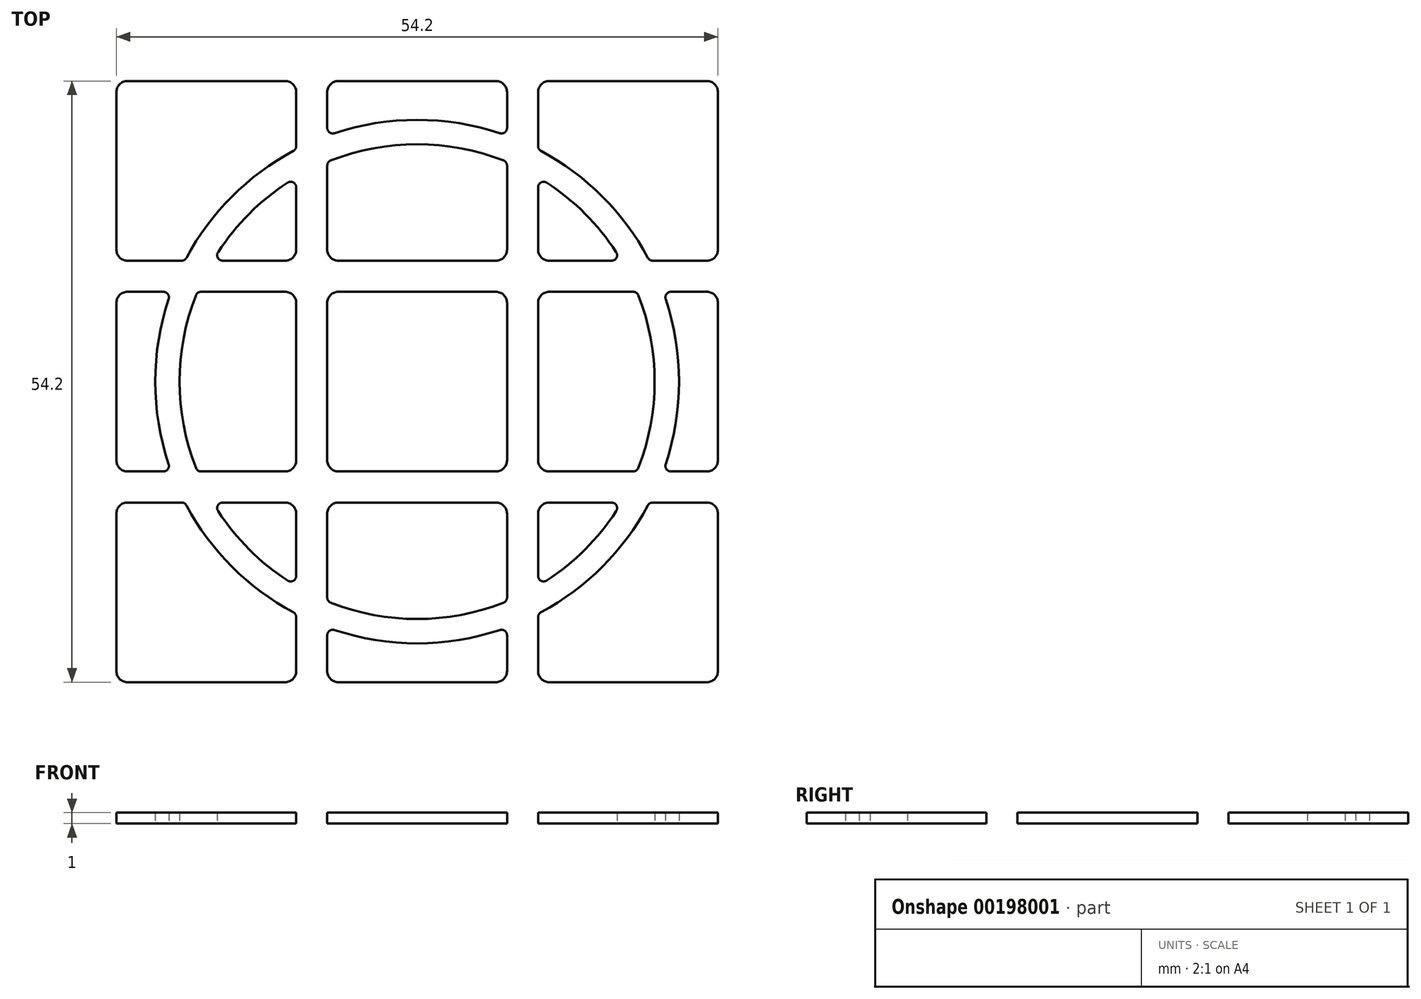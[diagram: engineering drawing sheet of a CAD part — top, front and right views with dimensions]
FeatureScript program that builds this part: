
annotation { "Feature Type Name" : "Feature", "Feature Type Description" : "" }
export const myFeature = defineFeature(function(context is Context, id is Id, definition is map)
    precondition{}
    {
        {
            var Q0;
            Q0=qCreatedBy(makeId("Top.planeOp"),FACE);
            var sketch = newSketch(context, id + "F0", { "sketchPlane" : qUnion([Q0])});
            skLineSegment(sketch, "E0.bottom", {"start": v(28.5, -28.5) * mm, "end": v(-28.5, -28.5) * mm, "construction": true});
            skLineSegment(sketch, "E0.top", {"start": v(28.5, 28.5) * mm, "end": v(-28.5, 28.5) * mm, "construction": true});
            skLineSegment(sketch, "E0.left", {"start": v(28.5, -28.5) * mm, "end": v(28.5, 28.5) * mm, "construction": true});
            skLineSegment(sketch, "E0.right", {"start": v(-28.5, -28.5) * mm, "end": v(-28.5, 28.5) * mm, "construction": true});
            skPoint(sketch, "E0.middle", {"position": v(0, 0) * mm});
            skLineSegment(sketch, "E1", {"start": v(-9.5, 28.5) * mm, "end": v(-9.5, -28.5) * mm, "construction": true});
            skLineSegment(sketch, "E2", {"start": v(9.5, -28.5) * mm, "end": v(9.5, 28.5) * mm, "construction": true});
            skLineSegment(sketch, "E3", {"start": v(-28.5, 9.5) * mm, "end": v(28.5, 9.5) * mm, "construction": true});
            skLineSegment(sketch, "E4", {"start": v(28.5, -9.5) * mm, "end": v(-28.5, -9.5) * mm, "construction": true});
            skArc(sketch, "E5", {"start": v(-11.16, 20.8) * mm, "mid": v(-16.69, 16.69) * mm, "end": v(-20.8, 11.16) * mm});
            skArc(sketch, "E6", {"start": v(-11.67, 17.94) * mm, "mid": v(-15.13, 15.13) * mm, "end": v(-17.94, 11.67) * mm});
            skLineSegment(sketch, "E7.bottom", {"start": v(-26.1, 27.1) * mm, "end": v(-11.9, 27.1) * mm});
            skLineSegment(sketch, "E7.top", {"start": v(-26.1, 10.9) * mm, "end": v(-21.23, 10.9) * mm});
            skLineSegment(sketch, "E7.left", {"start": v(-27.1, 26.1) * mm, "end": v(-27.1, 11.9) * mm});
            skLineSegment(sketch, "E7.right", {"start": v(-10.9, 26.1) * mm, "end": v(-10.9, 21.23) * mm});
            skLineSegment(sketch, "E8.bottom", {"start": v(-26.1, 8.1) * mm, "end": v(-22.87, 8.1) * mm});
            skLineSegment(sketch, "E8.top", {"start": v(-26.1, -8.1) * mm, "end": v(-22.87, -8.1) * mm});
            skLineSegment(sketch, "E8.left", {"start": v(-27.1, 7.1) * mm, "end": v(-27.1, -7.1) * mm});
            skLineSegment(sketch, "E8.right", {"start": v(-10.9, 7.1) * mm, "end": v(-10.9, -7.1) * mm});
            skPoint(sketch, "E9.visualSharp", {"position": v(-27.1, 27.1) * mm});
            skArc(sketch, "E9.filletArc", {"start": v(-26.1, 27.1) * mm, "mid": v(-26.8, 26.8) * mm, "end": v(-27.1, 26.1) * mm});
            skPoint(sketch, "E10.visualSharp", {"position": v(-10.9, 27.1) * mm});
            skArc(sketch, "E10.filletArc", {"start": v(-10.9, 26.1) * mm, "mid": v(-11.2, 26.8) * mm, "end": v(-11.9, 27.1) * mm});
            skPoint(sketch, "E11.visualSharp", {"position": v(-10.9, 10.9) * mm});
            skArc(sketch, "E11.filletArc", {"start": v(-11.9, 10.9) * mm, "mid": v(-11.2, 11.2) * mm, "end": v(-10.9, 11.9) * mm});
            skPoint(sketch, "E12.visualSharp", {"position": v(-27.1, 10.9) * mm});
            skArc(sketch, "E12.filletArc", {"start": v(-27.1, 11.9) * mm, "mid": v(-26.8, 11.2) * mm, "end": v(-26.1, 10.9) * mm});
            skPoint(sketch, "E13.visualSharp", {"position": v(-27.1, 8.1) * mm});
            skArc(sketch, "E13.filletArc", {"start": v(-26.1, 8.1) * mm, "mid": v(-26.8, 7.8) * mm, "end": v(-27.1, 7.1) * mm});
            skPoint(sketch, "E14.visualSharp", {"position": v(-27.1, -8.1) * mm});
            skArc(sketch, "E14.filletArc", {"start": v(-27.1, -7.1) * mm, "mid": v(-26.8, -7.8) * mm, "end": v(-26.1, -8.1) * mm});
            skPoint(sketch, "E15.visualSharp", {"position": v(-10.9, -8.1) * mm});
            skArc(sketch, "E15.filletArc", {"start": v(-11.9, -8.1) * mm, "mid": v(-11.2, -7.8) * mm, "end": v(-10.9, -7.1) * mm});
            skPoint(sketch, "E16.visualSharp", {"position": v(-10.9, 8.1) * mm});
            skArc(sketch, "E16.filletArc", {"start": v(-10.9, 7.1) * mm, "mid": v(-11.2, 7.8) * mm, "end": v(-11.9, 8.1) * mm});
            skLineSegment(sketch, "E17.trimOffspring", {"start": v(-10.9, 17.52) * mm, "end": v(-10.9, 11.9) * mm});
            skLineSegment(sketch, "E18.trimOffspring", {"start": v(-19.47, -8.1) * mm, "end": v(-11.9, -8.1) * mm});
            skLineSegment(sketch, "E19.trimOffspring", {"start": v(-19.47, 8.1) * mm, "end": v(-11.9, 8.1) * mm});
            skLineSegment(sketch, "E20.trimOffspring", {"start": v(-17.52, 10.9) * mm, "end": v(-11.9, 10.9) * mm});
            skArc(sketch, "E21.trimOffspring", {"start": v(-19.93, 7.78) * mm, "mid": v(-21.4, 0) * mm, "end": v(-19.93, -7.78) * mm});
            skArc(sketch, "E22.trimOffspring", {"start": v(-22.4, 7.44) * mm, "mid": v(-23.6, 0) * mm, "end": v(-22.4, -7.44) * mm});
            skPoint(sketch, "E23.visualSharp", {"position": v(-20.93, 10.9) * mm});
            skArc(sketch, "E23.filletArc", {"start": v(-21.23, 10.9) * mm, "mid": v(-20.98, 10.97) * mm, "end": v(-20.8, 11.16) * mm});
            skPoint(sketch, "E24.visualSharp", {"position": v(-10.9, 20.93) * mm});
            skArc(sketch, "E24.filletArc", {"start": v(-11.16, 20.8) * mm, "mid": v(-10.97, 20.98) * mm, "end": v(-10.9, 21.23) * mm});
            skPoint(sketch, "E25.visualSharp", {"position": v(-19.8, 8.1) * mm});
            skArc(sketch, "E25.filletArc", {"start": v(-19.47, 8.1) * mm, "mid": v(-19.75, 8.01) * mm, "end": v(-19.93, 7.78) * mm});
            skPoint(sketch, "E26.visualSharp", {"position": v(-19.8, -8.1) * mm});
            skArc(sketch, "E26.filletArc", {"start": v(-19.93, -7.78) * mm, "mid": v(-19.75, -8.01) * mm, "end": v(-19.47, -8.1) * mm});
            skPoint(sketch, "E27.visualSharp", {"position": v(-18.42, 10.9) * mm});
            skArc(sketch, "E27.filletArc", {"start": v(-17.94, 11.67) * mm, "mid": v(-17.96, 11.16) * mm, "end": v(-17.52, 10.9) * mm});
            skPoint(sketch, "E28.visualSharp", {"position": v(-10.9, 18.42) * mm});
            skArc(sketch, "E28.filletArc", {"start": v(-10.9, 17.52) * mm, "mid": v(-11.16, 17.96) * mm, "end": v(-11.67, 17.94) * mm});
            skPoint(sketch, "E29.visualSharp", {"position": v(-22.17, 8.1) * mm});
            skArc(sketch, "E29.filletArc", {"start": v(-22.4, 7.44) * mm, "mid": v(-22.46, 7.9) * mm, "end": v(-22.87, 8.1) * mm});
            skPoint(sketch, "E30.visualSharp", {"position": v(-22.17, -8.1) * mm});
            skArc(sketch, "E30.filletArc", {"start": v(-22.87, -8.1) * mm, "mid": v(-22.46, -7.9) * mm, "end": v(-22.4, -7.44) * mm});
            skArc(sketch, "E31.1.0", {"start": v(-20.8, -11.16) * mm, "mid": v(-16.69, -16.69) * mm, "end": v(-11.16, -20.8) * mm});
            skLineSegment(sketch, "E31.1.1", {"start": v(8.1, -19.47) * mm, "end": v(8.1, -11.9) * mm});
            skLineSegment(sketch, "E31.1.2", {"start": v(-27.1, -26.1) * mm, "end": v(-27.1, -11.9) * mm});
            skPoint(sketch, "E31.1.3", {"position": v(-8.1, -10.9) * mm});
            skLineSegment(sketch, "E31.1.4", {"start": v(-26.1, -27.1) * mm, "end": v(-11.9, -27.1) * mm});
            skArc(sketch, "E31.1.5", {"start": v(-17.94, -11.67) * mm, "mid": v(-15.13, -15.13) * mm, "end": v(-11.67, -17.94) * mm});
            skLineSegment(sketch, "E31.1.6", {"start": v(-8.1, -19.47) * mm, "end": v(-8.1, -11.9) * mm});
            skArc(sketch, "E31.1.7", {"start": v(-7.78, -19.93) * mm, "mid": v(0, -21.4) * mm, "end": v(7.78, -19.93) * mm});
            skPoint(sketch, "E31.1.8", {"position": v(-8.1, -22.17) * mm});
            skLineSegment(sketch, "E31.1.9", {"start": v(-10.9, -26.1) * mm, "end": v(-10.9, -21.23) * mm});
            skPoint(sketch, "E31.1.10", {"position": v(8.1, -19.8) * mm});
            skPoint(sketch, "E31.1.11", {"position": v(-8.1, -27.1) * mm});
            skLineSegment(sketch, "E31.1.12", {"start": v(-10.9, -17.52) * mm, "end": v(-10.9, -11.9) * mm});
            skLineSegment(sketch, "E31.1.13", {"start": v(-7.1, -27.1) * mm, "end": v(7.1, -27.1) * mm});
            skPoint(sketch, "E31.1.14", {"position": v(-27.1, -10.9) * mm});
            skPoint(sketch, "E31.1.15", {"position": v(-20.93, -10.9) * mm});
            skPoint(sketch, "E31.1.16", {"position": v(-10.9, -10.9) * mm});
            skPoint(sketch, "E31.1.17", {"position": v(8.1, -27.1) * mm});
            skLineSegment(sketch, "E31.1.18", {"start": v(-7.1, -10.9) * mm, "end": v(7.1, -10.9) * mm});
            skPoint(sketch, "E31.1.19", {"position": v(-10.9, -20.93) * mm});
            skPoint(sketch, "E31.1.20", {"position": v(-10.9, -18.42) * mm});
            skPoint(sketch, "E31.1.21", {"position": v(-18.42, -10.9) * mm});
            skPoint(sketch, "E31.1.22", {"position": v(8.1, -10.9) * mm});
            skLineSegment(sketch, "E31.1.23", {"start": v(8.1, -26.1) * mm, "end": v(8.1, -22.87) * mm});
            skLineSegment(sketch, "E31.1.24", {"start": v(-8.1, -26.1) * mm, "end": v(-8.1, -22.87) * mm});
            skLineSegment(sketch, "E31.1.25", {"start": v(-26.1, -10.9) * mm, "end": v(-21.23, -10.9) * mm});
            skArc(sketch, "E31.1.26", {"start": v(-7.44, -22.4) * mm, "mid": v(0, -23.6) * mm, "end": v(7.44, -22.4) * mm});
            skLineSegment(sketch, "E31.1.27", {"start": v(-17.52, -10.9) * mm, "end": v(-11.9, -10.9) * mm});
            skPoint(sketch, "E31.1.28", {"position": v(-27.1, -27.1) * mm});
            skPoint(sketch, "E31.1.29", {"position": v(-8.1, -19.8) * mm});
            skPoint(sketch, "E31.1.30", {"position": v(-10.9, -27.1) * mm});
            skPoint(sketch, "E31.1.31", {"position": v(8.1, -22.17) * mm});
            skArc(sketch, "E31.1.32", {"start": v(8.1, -11.9) * mm, "mid": v(7.8, -11.2) * mm, "end": v(7.1, -10.9) * mm});
            skArc(sketch, "E31.1.33", {"start": v(7.1, -27.1) * mm, "mid": v(7.8, -26.8) * mm, "end": v(8.1, -26.1) * mm});
            skArc(sketch, "E31.1.34", {"start": v(-11.9, -27.1) * mm, "mid": v(-11.2, -26.8) * mm, "end": v(-10.9, -26.1) * mm});
            skArc(sketch, "E31.1.35", {"start": v(-10.9, -11.9) * mm, "mid": v(-11.2, -11.2) * mm, "end": v(-11.9, -10.9) * mm});
            skArc(sketch, "E31.1.36", {"start": v(-8.1, -26.1) * mm, "mid": v(-7.8, -26.8) * mm, "end": v(-7.1, -27.1) * mm});
            skArc(sketch, "E31.1.37", {"start": v(-7.1, -10.9) * mm, "mid": v(-7.8, -11.2) * mm, "end": v(-8.1, -11.9) * mm});
            skArc(sketch, "E31.1.38", {"start": v(-27.1, -26.1) * mm, "mid": v(-26.8, -26.8) * mm, "end": v(-26.1, -27.1) * mm});
            skArc(sketch, "E31.1.39", {"start": v(-26.1, -10.9) * mm, "mid": v(-26.8, -11.2) * mm, "end": v(-27.1, -11.9) * mm});
            skArc(sketch, "E31.1.40", {"start": v(8.1, -22.87) * mm, "mid": v(7.9, -22.46) * mm, "end": v(7.44, -22.4) * mm});
            skArc(sketch, "E31.1.41", {"start": v(-11.67, -17.94) * mm, "mid": v(-11.16, -17.96) * mm, "end": v(-10.9, -17.52) * mm});
            skArc(sketch, "E31.1.42", {"start": v(-17.52, -10.9) * mm, "mid": v(-17.96, -11.16) * mm, "end": v(-17.94, -11.67) * mm});
            skArc(sketch, "E31.1.43", {"start": v(-7.44, -22.4) * mm, "mid": v(-7.9, -22.46) * mm, "end": v(-8.1, -22.87) * mm});
            skArc(sketch, "E31.1.44", {"start": v(-10.9, -21.23) * mm, "mid": v(-10.97, -20.98) * mm, "end": v(-11.16, -20.8) * mm});
            skArc(sketch, "E31.1.45", {"start": v(-20.8, -11.16) * mm, "mid": v(-20.98, -10.97) * mm, "end": v(-21.23, -10.9) * mm});
            skArc(sketch, "E31.1.46", {"start": v(7.78, -19.93) * mm, "mid": v(8.01, -19.75) * mm, "end": v(8.1, -19.47) * mm});
            skArc(sketch, "E31.1.47", {"start": v(-8.1, -19.47) * mm, "mid": v(-8.01, -19.75) * mm, "end": v(-7.78, -19.93) * mm});
            skArc(sketch, "E31.2.0", {"start": v(11.16, -20.8) * mm, "mid": v(16.69, -16.69) * mm, "end": v(20.8, -11.16) * mm});
            skLineSegment(sketch, "E31.2.1", {"start": v(19.47, 8.1) * mm, "end": v(11.9, 8.1) * mm});
            skLineSegment(sketch, "E31.2.2", {"start": v(26.1, -27.1) * mm, "end": v(11.9, -27.1) * mm});
            skPoint(sketch, "E31.2.3", {"position": v(10.9, -8.1) * mm});
            skLineSegment(sketch, "E31.2.4", {"start": v(27.1, -26.1) * mm, "end": v(27.1, -11.9) * mm});
            skArc(sketch, "E31.2.5", {"start": v(11.67, -17.94) * mm, "mid": v(15.13, -15.13) * mm, "end": v(17.94, -11.67) * mm});
            skLineSegment(sketch, "E31.2.6", {"start": v(19.47, -8.1) * mm, "end": v(11.9, -8.1) * mm});
            skArc(sketch, "E31.2.7", {"start": v(19.93, -7.78) * mm, "mid": v(21.4, 0) * mm, "end": v(19.93, 7.78) * mm});
            skPoint(sketch, "E31.2.8", {"position": v(22.17, -8.1) * mm});
            skLineSegment(sketch, "E31.2.9", {"start": v(26.1, -10.9) * mm, "end": v(21.23, -10.9) * mm});
            skPoint(sketch, "E31.2.10", {"position": v(19.8, 8.1) * mm});
            skPoint(sketch, "E31.2.11", {"position": v(27.1, -8.1) * mm});
            skLineSegment(sketch, "E31.2.12", {"start": v(17.52, -10.9) * mm, "end": v(11.9, -10.9) * mm});
            skLineSegment(sketch, "E31.2.13", {"start": v(27.1, -7.1) * mm, "end": v(27.1, 7.1) * mm});
            skPoint(sketch, "E31.2.14", {"position": v(10.9, -27.1) * mm});
            skPoint(sketch, "E31.2.15", {"position": v(10.9, -20.93) * mm});
            skPoint(sketch, "E31.2.16", {"position": v(10.9, -10.9) * mm});
            skPoint(sketch, "E31.2.17", {"position": v(27.1, 8.1) * mm});
            skLineSegment(sketch, "E31.2.18", {"start": v(10.9, -7.1) * mm, "end": v(10.9, 7.1) * mm});
            skPoint(sketch, "E31.2.19", {"position": v(20.93, -10.9) * mm});
            skPoint(sketch, "E31.2.20", {"position": v(18.42, -10.9) * mm});
            skPoint(sketch, "E31.2.21", {"position": v(10.9, -18.42) * mm});
            skPoint(sketch, "E31.2.22", {"position": v(10.9, 8.1) * mm});
            skLineSegment(sketch, "E31.2.23", {"start": v(26.1, 8.1) * mm, "end": v(22.87, 8.1) * mm});
            skLineSegment(sketch, "E31.2.24", {"start": v(26.1, -8.1) * mm, "end": v(22.87, -8.1) * mm});
            skLineSegment(sketch, "E31.2.25", {"start": v(10.9, -26.1) * mm, "end": v(10.9, -21.23) * mm});
            skArc(sketch, "E31.2.26", {"start": v(22.4, -7.44) * mm, "mid": v(23.6, 0) * mm, "end": v(22.4, 7.44) * mm});
            skLineSegment(sketch, "E31.2.27", {"start": v(10.9, -17.52) * mm, "end": v(10.9, -11.9) * mm});
            skPoint(sketch, "E31.2.28", {"position": v(27.1, -27.1) * mm});
            skPoint(sketch, "E31.2.29", {"position": v(19.8, -8.1) * mm});
            skPoint(sketch, "E31.2.30", {"position": v(27.1, -10.9) * mm});
            skPoint(sketch, "E31.2.31", {"position": v(22.17, 8.1) * mm});
            skArc(sketch, "E31.2.32", {"start": v(11.9, 8.1) * mm, "mid": v(11.2, 7.8) * mm, "end": v(10.9, 7.1) * mm});
            skArc(sketch, "E31.2.33", {"start": v(27.1, 7.1) * mm, "mid": v(26.8, 7.8) * mm, "end": v(26.1, 8.1) * mm});
            skArc(sketch, "E31.2.34", {"start": v(27.1, -11.9) * mm, "mid": v(26.8, -11.2) * mm, "end": v(26.1, -10.9) * mm});
            skArc(sketch, "E31.2.35", {"start": v(11.9, -10.9) * mm, "mid": v(11.2, -11.2) * mm, "end": v(10.9, -11.9) * mm});
            skArc(sketch, "E31.2.36", {"start": v(26.1, -8.1) * mm, "mid": v(26.8, -7.8) * mm, "end": v(27.1, -7.1) * mm});
            skArc(sketch, "E31.2.37", {"start": v(10.9, -7.1) * mm, "mid": v(11.2, -7.8) * mm, "end": v(11.9, -8.1) * mm});
            skArc(sketch, "E31.2.38", {"start": v(26.1, -27.1) * mm, "mid": v(26.8, -26.8) * mm, "end": v(27.1, -26.1) * mm});
            skArc(sketch, "E31.2.39", {"start": v(10.9, -26.1) * mm, "mid": v(11.2, -26.8) * mm, "end": v(11.9, -27.1) * mm});
            skArc(sketch, "E31.2.40", {"start": v(22.87, 8.1) * mm, "mid": v(22.46, 7.9) * mm, "end": v(22.4, 7.44) * mm});
            skArc(sketch, "E31.2.41", {"start": v(17.94, -11.67) * mm, "mid": v(17.96, -11.16) * mm, "end": v(17.52, -10.9) * mm});
            skArc(sketch, "E31.2.42", {"start": v(10.9, -17.52) * mm, "mid": v(11.16, -17.96) * mm, "end": v(11.67, -17.94) * mm});
            skArc(sketch, "E31.2.43", {"start": v(22.4, -7.44) * mm, "mid": v(22.46, -7.9) * mm, "end": v(22.87, -8.1) * mm});
            skArc(sketch, "E31.2.44", {"start": v(21.23, -10.9) * mm, "mid": v(20.98, -10.97) * mm, "end": v(20.8, -11.16) * mm});
            skArc(sketch, "E31.2.45", {"start": v(11.16, -20.8) * mm, "mid": v(10.97, -20.98) * mm, "end": v(10.9, -21.23) * mm});
            skArc(sketch, "E31.2.46", {"start": v(19.93, 7.78) * mm, "mid": v(19.75, 8.01) * mm, "end": v(19.47, 8.1) * mm});
            skArc(sketch, "E31.2.47", {"start": v(19.47, -8.1) * mm, "mid": v(19.75, -8.01) * mm, "end": v(19.93, -7.78) * mm});
            skArc(sketch, "E31.3.0", {"start": v(20.8, 11.16) * mm, "mid": v(16.69, 16.69) * mm, "end": v(11.16, 20.8) * mm});
            skLineSegment(sketch, "E31.3.1", {"start": v(-8.1, 19.47) * mm, "end": v(-8.1, 11.9) * mm});
            skLineSegment(sketch, "E31.3.2", {"start": v(27.1, 26.1) * mm, "end": v(27.1, 11.9) * mm});
            skPoint(sketch, "E31.3.3", {"position": v(8.1, 10.9) * mm});
            skLineSegment(sketch, "E31.3.4", {"start": v(26.1, 27.1) * mm, "end": v(11.9, 27.1) * mm});
            skArc(sketch, "E31.3.5", {"start": v(17.94, 11.67) * mm, "mid": v(15.13, 15.13) * mm, "end": v(11.67, 17.94) * mm});
            skLineSegment(sketch, "E31.3.6", {"start": v(8.1, 19.47) * mm, "end": v(8.1, 11.9) * mm});
            skArc(sketch, "E31.3.7", {"start": v(7.78, 19.93) * mm, "mid": v(0, 21.4) * mm, "end": v(-7.78, 19.93) * mm});
            skPoint(sketch, "E31.3.8", {"position": v(8.1, 22.17) * mm});
            skLineSegment(sketch, "E31.3.9", {"start": v(10.9, 26.1) * mm, "end": v(10.9, 21.23) * mm});
            skPoint(sketch, "E31.3.10", {"position": v(-8.1, 19.8) * mm});
            skPoint(sketch, "E31.3.11", {"position": v(8.1, 27.1) * mm});
            skLineSegment(sketch, "E31.3.12", {"start": v(10.9, 17.52) * mm, "end": v(10.9, 11.9) * mm});
            skLineSegment(sketch, "E31.3.13", {"start": v(7.1, 27.1) * mm, "end": v(-7.1, 27.1) * mm});
            skPoint(sketch, "E31.3.14", {"position": v(27.1, 10.9) * mm});
            skPoint(sketch, "E31.3.15", {"position": v(20.93, 10.9) * mm});
            skPoint(sketch, "E31.3.16", {"position": v(10.9, 10.9) * mm});
            skPoint(sketch, "E31.3.17", {"position": v(-8.1, 27.1) * mm});
            skLineSegment(sketch, "E31.3.18", {"start": v(7.1, 10.9) * mm, "end": v(-7.1, 10.9) * mm});
            skPoint(sketch, "E31.3.19", {"position": v(10.9, 20.93) * mm});
            skPoint(sketch, "E31.3.20", {"position": v(10.9, 18.42) * mm});
            skPoint(sketch, "E31.3.21", {"position": v(18.42, 10.9) * mm});
            skPoint(sketch, "E31.3.22", {"position": v(-8.1, 10.9) * mm});
            skLineSegment(sketch, "E31.3.23", {"start": v(-8.1, 26.1) * mm, "end": v(-8.1, 22.87) * mm});
            skLineSegment(sketch, "E31.3.24", {"start": v(8.1, 26.1) * mm, "end": v(8.1, 22.87) * mm});
            skLineSegment(sketch, "E31.3.25", {"start": v(26.1, 10.9) * mm, "end": v(21.23, 10.9) * mm});
            skArc(sketch, "E31.3.26", {"start": v(7.44, 22.4) * mm, "mid": v(0, 23.6) * mm, "end": v(-7.44, 22.4) * mm});
            skLineSegment(sketch, "E31.3.27", {"start": v(17.52, 10.9) * mm, "end": v(11.9, 10.9) * mm});
            skPoint(sketch, "E31.3.28", {"position": v(27.1, 27.1) * mm});
            skPoint(sketch, "E31.3.29", {"position": v(8.1, 19.8) * mm});
            skPoint(sketch, "E31.3.30", {"position": v(10.9, 27.1) * mm});
            skPoint(sketch, "E31.3.31", {"position": v(-8.1, 22.17) * mm});
            skArc(sketch, "E31.3.32", {"start": v(-8.1, 11.9) * mm, "mid": v(-7.8, 11.2) * mm, "end": v(-7.1, 10.9) * mm});
            skArc(sketch, "E31.3.33", {"start": v(-7.1, 27.1) * mm, "mid": v(-7.8, 26.8) * mm, "end": v(-8.1, 26.1) * mm});
            skArc(sketch, "E31.3.34", {"start": v(11.9, 27.1) * mm, "mid": v(11.2, 26.8) * mm, "end": v(10.9, 26.1) * mm});
            skArc(sketch, "E31.3.35", {"start": v(10.9, 11.9) * mm, "mid": v(11.2, 11.2) * mm, "end": v(11.9, 10.9) * mm});
            skArc(sketch, "E31.3.36", {"start": v(8.1, 26.1) * mm, "mid": v(7.8, 26.8) * mm, "end": v(7.1, 27.1) * mm});
            skArc(sketch, "E31.3.37", {"start": v(7.1, 10.9) * mm, "mid": v(7.8, 11.2) * mm, "end": v(8.1, 11.9) * mm});
            skArc(sketch, "E31.3.38", {"start": v(27.1, 26.1) * mm, "mid": v(26.8, 26.8) * mm, "end": v(26.1, 27.1) * mm});
            skArc(sketch, "E31.3.39", {"start": v(26.1, 10.9) * mm, "mid": v(26.8, 11.2) * mm, "end": v(27.1, 11.9) * mm});
            skArc(sketch, "E31.3.40", {"start": v(-8.1, 22.87) * mm, "mid": v(-7.9, 22.46) * mm, "end": v(-7.44, 22.4) * mm});
            skArc(sketch, "E31.3.41", {"start": v(11.67, 17.94) * mm, "mid": v(11.16, 17.96) * mm, "end": v(10.9, 17.52) * mm});
            skArc(sketch, "E31.3.42", {"start": v(17.52, 10.9) * mm, "mid": v(17.96, 11.16) * mm, "end": v(17.94, 11.67) * mm});
            skArc(sketch, "E31.3.43", {"start": v(7.44, 22.4) * mm, "mid": v(7.9, 22.46) * mm, "end": v(8.1, 22.87) * mm});
            skArc(sketch, "E31.3.44", {"start": v(10.9, 21.23) * mm, "mid": v(10.97, 20.98) * mm, "end": v(11.16, 20.8) * mm});
            skArc(sketch, "E31.3.45", {"start": v(20.8, 11.16) * mm, "mid": v(20.98, 10.97) * mm, "end": v(21.23, 10.9) * mm});
            skArc(sketch, "E31.3.46", {"start": v(-7.78, 19.93) * mm, "mid": v(-8.01, 19.75) * mm, "end": v(-8.1, 19.47) * mm});
            skArc(sketch, "E31.3.47", {"start": v(8.1, 19.47) * mm, "mid": v(8.01, 19.75) * mm, "end": v(7.78, 19.93) * mm});
            skLineSegment(sketch, "E32.bottom", {"start": v(-7.1, 8.1) * mm, "end": v(7.1, 8.1) * mm});
            skLineSegment(sketch, "E32.top", {"start": v(-7.1, -8.1) * mm, "end": v(7.1, -8.1) * mm});
            skLineSegment(sketch, "E32.left", {"start": v(-8.1, 7.1) * mm, "end": v(-8.1, -7.1) * mm});
            skLineSegment(sketch, "E32.right", {"start": v(8.1, 7.1) * mm, "end": v(8.1, -7.1) * mm});
            skPoint(sketch, "E33.visualSharp", {"position": v(-8.1, 8.1) * mm});
            skArc(sketch, "E33.filletArc", {"start": v(-7.1, 8.1) * mm, "mid": v(-7.8, 7.8) * mm, "end": v(-8.1, 7.1) * mm});
            skPoint(sketch, "E34.visualSharp", {"position": v(8.1, 8.1) * mm});
            skArc(sketch, "E34.filletArc", {"start": v(8.1, 7.1) * mm, "mid": v(7.8, 7.8) * mm, "end": v(7.1, 8.1) * mm});
            skPoint(sketch, "E35.visualSharp", {"position": v(8.1, -8.1) * mm});
            skArc(sketch, "E35.filletArc", {"start": v(7.1, -8.1) * mm, "mid": v(7.8, -7.8) * mm, "end": v(8.1, -7.1) * mm});
            skPoint(sketch, "E36.visualSharp", {"position": v(-8.1, -8.1) * mm});
            skArc(sketch, "E36.filletArc", {"start": v(-8.1, -7.1) * mm, "mid": v(-7.8, -7.8) * mm, "end": v(-7.1, -8.1) * mm});
            skSolve(sketch);
        }
        {
            var Q0;
            Q0 = qSketchRegion(id + "F0", true);
            extrude(context, id + "F1", {"entities" : qUnion([Q0]), "depth" : 1 * mm});
        }
    });
